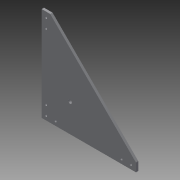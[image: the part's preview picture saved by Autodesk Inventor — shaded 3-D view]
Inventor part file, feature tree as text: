
AUTODESK INVENTOR PART (.ipt)
format: ipt  version: 2013 (Build 170138000, 138)  size: 82,944 bytes
history: native  units: in
note: dims shown in document units (in); Inventor stores cm internally (conversion verified against a paired STEP export)
features: extrude x1, hole x1, sketch x1
ambient origin geometry x8: Origin, YZ Plane, XZ Plane, XY Plane, X Axis, Y Axis, Z Axis, Center Point
bodies: Solid1 (feature_tree)
feature tree (3):
  extrude  "Extrusion1"  [1 undecoded]
  hole  "Hole1"  [1 undecoded]
  sketch  "Sketch1"  dims[d0=0.1969in d1=0.0in d2=2.3622in d3=2.3622in d4=0.3051in d5=0.2362in d6=0.1575in d7=0.0787in d8=90.0deg d9=0.315in d10=0.8108in]
note: 2 required parameter values undecoded (feature->parameter linkage not recoverable at this tier; creation-order binding heuristic only, values carry confidence <= 0.55)
